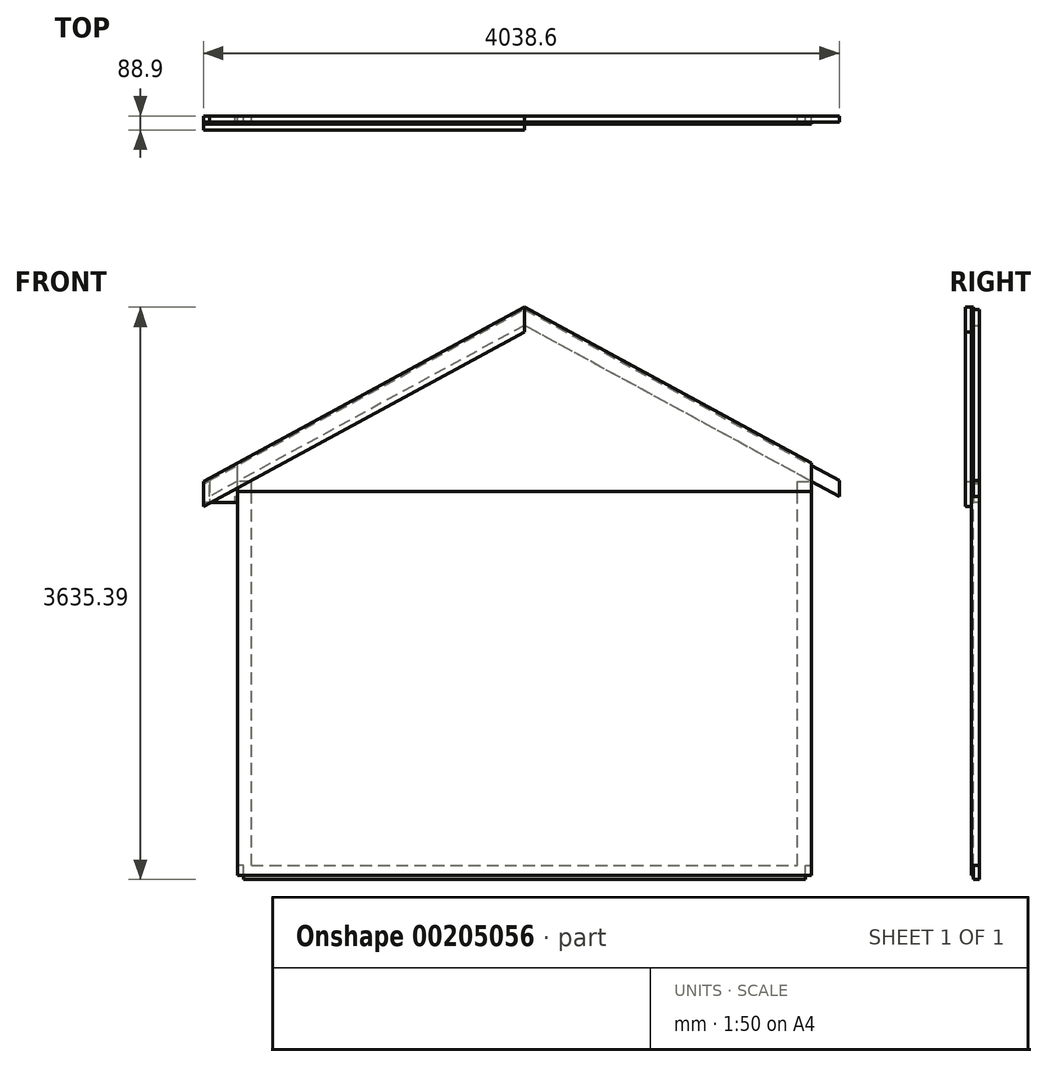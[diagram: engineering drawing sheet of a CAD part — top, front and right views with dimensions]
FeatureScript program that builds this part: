
annotation { "Feature Type Name" : "Feature", "Feature Type Description" : "" }
export const myFeature = defineFeature(function(context is Context, id is Id, definition is map)
    precondition{}
    {
        {
            var Q0;
            Q0=qCreatedBy(makeId("Front.planeOp"),FACE);
            var sketch = newSketch(context, id + "F0", { "sketchPlane" : qUnion([Q0])});
            skLineSegment(sketch, "E0.bottom", {"start": v(-1784.35, 0) * mm, "end": v(1784.35, 0) * mm});
            skLineSegment(sketch, "E0.top", {"start": v(-1784.35, 88.9) * mm, "end": v(1784.35, 88.9) * mm});
            skLineSegment(sketch, "E0.left", {"start": v(-1784.35, 0) * mm, "end": v(-1784.35, 88.9) * mm});
            skLineSegment(sketch, "E0.right", {"start": v(1784.35, 0) * mm, "end": v(1784.35, 88.9) * mm});
            skLineSegment(sketch, "E1.bottom", {"start": v(1733.55, 88.9) * mm, "end": v(1822.45, 88.9) * mm});
            skLineSegment(sketch, "E1.top", {"start": v(1733.55, 2528.73) * mm, "end": v(1822.45, 2528.73) * mm});
            skLineSegment(sketch, "E1.left", {"start": v(1733.55, 88.9) * mm, "end": v(1733.55, 2528.73) * mm});
            skLineSegment(sketch, "E1.right", {"start": v(1822.45, 88.9) * mm, "end": v(1822.45, 2528.73) * mm});
            skLineSegment(sketch, "E2.bottom", {"start": v(-1733.55, 88.9) * mm, "end": v(-1822.45, 88.9) * mm});
            skLineSegment(sketch, "E2.top", {"start": v(-1733.55, 2528.73) * mm, "end": v(-1822.45, 2528.73) * mm});
            skLineSegment(sketch, "E2.left", {"start": v(-1733.55, 88.9) * mm, "end": v(-1733.55, 2528.73) * mm});
            skLineSegment(sketch, "E2.right", {"start": v(-1822.45, 88.9) * mm, "end": v(-1822.45, 2528.73) * mm});
            skLineSegment(sketch, "E3", {"start": v(0, 3620.93) * mm, "end": v(2000.25, 2533.24) * mm});
            skLineSegment(sketch, "E4", {"start": v(2000.25, 2533.24) * mm, "end": v(2000.25, 2432.05) * mm});
            skLineSegment(sketch, "E5", {"start": v(2000.25, 2432.05) * mm, "end": v(0, 3519.74) * mm});
            skLineSegment(sketch, "E6", {"start": v(0, 3519.74) * mm, "end": v(-2000.25, 2432.05) * mm});
            skLineSegment(sketch, "E7", {"start": v(-2000.25, 2432.05) * mm, "end": v(-2000.25, 2533.24) * mm});
            skLineSegment(sketch, "E8", {"start": v(-2000.25, 2533.24) * mm, "end": v(0, 3620.93) * mm});
            skSolve(sketch);
        }
        {
            var Q0;
            Q0=makeQuery(id+"F0.imprint","IMPRINT",FACE,{"disambiguationData":[TD([[makeQuery(id+"F0.imprint","IMPRINT",EDGE,{"derivedFrom":sQuery(id+"F0.wireOp",EDGE,"E3")}),-1.0]])]});
            var Q1;
            Q1=makeQuery(id+"F0.imprint","IMPRINT",FACE,{"disambiguationData":[TD([[makeQuery(id+"F0.imprint","IMPRINT",EDGE,{"derivedFrom":sQuery(id+"F0.wireOp",EDGE,"E1.top")}),-1.0]])]});
            var Q2;
            Q2=makeQuery(id+"F0.imprint","IMPRINT",FACE,{"disambiguationData":[TD([[makeQuery(id+"F0.imprint","IMPRINT",EDGE,{"derivedFrom":sQuery(id+"F0.wireOp",EDGE,"E2.top")}),1.0]])]});
            var Q3;
            Q3=makeQuery(id+"F0.imprint","IMPRINT",FACE,{"disambiguationData":[TD([[makeQuery(id+"F0.imprint","IMPRINT",EDGE,{"derivedFrom":sQuery(id+"F0.wireOp",EDGE,"E0.bottom")}),1.0]])]});
            extrude(context, id + "F1", {"entities" : qUnion([Q0, Q1, Q2, Q3]), "depth" : 38.1 * mm});
        }
        {
            var Q0;
            Q0=makeQuery(id+"F1.opExtrude","CAP_FACE",FACE,{"disambiguationData":[OSD([sQuery(id+"F0.wireOp",EDGE,"E0.bottom"),sQuery(id+"F0.wireOp",EDGE,"E0.top"),sQuery(id+"F0.wireOp",EDGE,"E0.left"),sQuery(id+"F0.wireOp",EDGE,"E0.right"),sQuery(id+"F0.wireOp",EDGE,"E1.bottom"),sQuery(id+"F0.wireOp",EDGE,"E1.top"),sQuery(id+"F0.wireOp",EDGE,"E1.left"),sQuery(id+"F0.wireOp",EDGE,"E1.right"),sQuery(id+"F0.wireOp",EDGE,"E2.bottom"),sQuery(id+"F0.wireOp",EDGE,"E2.top"),sQuery(id+"F0.wireOp",EDGE,"E2.left"),sQuery(id+"F0.wireOp",EDGE,"E2.right")])],"isStart":false});
            var sketch = newSketch(context, id + "F2", { "sketchPlane" : qUnion([Q0])});
            skLineSegment(sketch, "E9.bottom", {"start": v(-1822.45, 25.4) * mm, "end": v(1822.45, 25.4) * mm});
            skLineSegment(sketch, "E9.top", {"start": v(-1822.45, 2463.8) * mm, "end": v(1822.45, 2463.8) * mm});
            skLineSegment(sketch, "E9.left", {"start": v(-1822.45, 25.4) * mm, "end": v(-1822.45, 2463.8) * mm});
            skLineSegment(sketch, "E9.right", {"start": v(1822.45, 25.4) * mm, "end": v(1822.45, 2463.8) * mm});
            skSolve(sketch);
        }
        {
            var Q0;
            Q0 = qSketchRegion(id + "F2", true);
            extrude(context, id + "F3", {"entities" : qUnion([Q0]), "depth" : 12.7 * mm});
        }
        {
            var Q0;
            Q0=makeQuery(id+"F1.opExtrude","CAP_FACE",FACE,{"disambiguationData":[OSD([sQuery(id+"F0.wireOp",EDGE,"E3"),sQuery(id+"F0.wireOp",EDGE,"E4"),sQuery(id+"F0.wireOp",EDGE,"E5"),sQuery(id+"F0.wireOp",EDGE,"E6"),sQuery(id+"F0.wireOp",EDGE,"E7"),sQuery(id+"F0.wireOp",EDGE,"E8")])],"isStart":false});
            var sketch = newSketch(context, id + "F4", { "sketchPlane" : qUnion([Q0])});
            skLineSegment(sketch, "E10", {"start": v(-1822.45, 2463.8) * mm, "end": v(-1822.45, 2644.38) * mm});
            skLineSegment(sketch, "E11", {"start": v(-1822.45, 2644.38) * mm, "end": v(0, 3635.39) * mm});
            skLineSegment(sketch, "E12", {"start": v(0, 3635.39) * mm, "end": v(1822.45, 2644.38) * mm});
            skLineSegment(sketch, "E13", {"start": v(1822.45, 2644.38) * mm, "end": v(1822.45, 2463.8) * mm});
            skLineSegment(sketch, "E14", {"start": v(1822.45, 2463.8) * mm, "end": v(-1822.45, 2463.8) * mm});
            skSolve(sketch);
        }
        {
            var Q0;
            Q0 = qSketchRegion(id + "F4", true);
            extrude(context, id + "F5", {"entities" : qUnion([Q0]), "depth" : 12.7 * mm});
        }
        {
            var Q0;
            Q0=makeQuery(id+"F1.opExtrude","CAP_FACE",FACE,{"disambiguationData":[OSD([sQuery(id+"F0.wireOp",EDGE,"E3"),sQuery(id+"F0.wireOp",EDGE,"E4"),sQuery(id+"F0.wireOp",EDGE,"E5"),sQuery(id+"F0.wireOp",EDGE,"E6"),sQuery(id+"F0.wireOp",EDGE,"E7"),sQuery(id+"F0.wireOp",EDGE,"E8")])],"isStart":false});
            var sketch = newSketch(context, id + "F6", { "sketchPlane" : qUnion([Q0])});
            skLineSegment(sketch, "E15", {"start": v(-2000.25, 2533.24) * mm, "end": v(-2000.25, 2393.54) * mm});
            skLineSegment(sketch, "E16", {"start": v(-2000.25, 2393.54) * mm, "end": v(-2038.35, 2393.54) * mm});
            skLineSegment(sketch, "E17", {"start": v(-2038.35, 2393.54) * mm, "end": v(-2038.35, 2512.53) * mm});
            skLineSegment(sketch, "E18", {"start": v(-2038.35, 2512.53) * mm, "end": v(-2000.25, 2533.24) * mm});
            skSolve(sketch);
        }
        {
            var Q0;
            Q0 = qSketchRegion(id + "F6", true);
            extrude(context, id + "F7", {"entities" : qUnion([Q0]), "oppositeDirection" : true, "depth" : 38.1 * mm});
        }
        {
            var Q0;
            Q0=makeQuery(id+"F7.boolean.opBoolean","MERGE",FACE,{"derivedFrom":[makeQuery(id+"F1.opExtrude","CAP_FACE",FACE,{"disambiguationData":[OSD([sQuery(id+"F0.wireOp",EDGE,"E3"),sQuery(id+"F0.wireOp",EDGE,"E4"),sQuery(id+"F0.wireOp",EDGE,"E5"),sQuery(id+"F0.wireOp",EDGE,"E6"),sQuery(id+"F0.wireOp",EDGE,"E7"),sQuery(id+"F0.wireOp",EDGE,"E8")])],"isStart":false}),makeQuery(id+"F7.opExtrude","CAP_FACE",FACE,{"disambiguationData":[OSD([sQuery(id+"F6.wireOp",EDGE,"E15"),sQuery(id+"F6.wireOp",EDGE,"E16"),sQuery(id+"F6.wireOp",EDGE,"E17"),sQuery(id+"F6.wireOp",EDGE,"E18")])],"isStart":true})]});
            var sketch = newSketch(context, id + "F8", { "sketchPlane" : qUnion([Q0])});
            skLineSegment(sketch, "E19.bottom", {"start": v(-1841.5, 2431.64) * mm, "end": v(-1822.45, 2431.64) * mm});
            skLineSegment(sketch, "E19.top", {"start": v(-1841.5, 2393.54) * mm, "end": v(-1822.45, 2393.54) * mm});
            skLineSegment(sketch, "E19.left", {"start": v(-1841.5, 2431.64) * mm, "end": v(-1841.5, 2393.54) * mm});
            skLineSegment(sketch, "E19.right", {"start": v(-1822.45, 2431.64) * mm, "end": v(-1822.45, 2393.54) * mm});
            skSolve(sketch);
        }
        {
            var Q0;
            Q0 = qSketchRegion(id + "F8", true);
            extrude(context, id + "F9", {"entities" : qUnion([Q0]), "operationType" : NewBodyOperationType.ADD, "oppositeDirection" : true, "depth" : 38.1 * mm});
        }
        {
            var Q0;
            Q0=makeQuery(id+"F5.opExtrude","CAP_FACE",FACE,{"disambiguationData":[OSD([sQuery(id+"F4.wireOp",EDGE,"E10"),sQuery(id+"F4.wireOp",EDGE,"E11"),sQuery(id+"F4.wireOp",EDGE,"E12"),sQuery(id+"F4.wireOp",EDGE,"E13"),sQuery(id+"F4.wireOp",EDGE,"E14")])],"isStart":false});
            var sketch = newSketch(context, id + "F10", { "sketchPlane" : qUnion([Q0])});
            skLineSegment(sketch, "E20", {"start": v(0, 3635.39) * mm, "end": v(0, 3476.37) * mm});
            skLineSegment(sketch, "E21", {"start": v(0, 3476.37) * mm, "end": v(-2038.35, 2367.96) * mm});
            skLineSegment(sketch, "E22", {"start": v(-2038.35, 2367.96) * mm, "end": v(-2038.35, 2526.98) * mm});
            skLineSegment(sketch, "E23", {"start": v(-2038.35, 2526.98) * mm, "end": v(0, 3635.39) * mm});
            skSolve(sketch);
        }
        {
            var Q0;
            Q0 = qSketchRegion(id + "F10", true);
            extrude(context, id + "F11", {"entities" : qUnion([Q0]), "depth" : 38.1 * mm});
        }
        {
            var Q0;
            Q0=makeQuery(id+"F7.opExtrude","CAP_FACE",FACE,{"disambiguationData":[OSD([sQuery(id+"F6.wireOp",EDGE,"E15"),sQuery(id+"F6.wireOp",EDGE,"E16"),sQuery(id+"F6.wireOp",EDGE,"E17"),sQuery(id+"F6.wireOp",EDGE,"E18")])],"isStart":true});
            var sketch = newSketch(context, id + "F12", { "sketchPlane" : qUnion([Q0])});
            skLineSegment(sketch, "E24", {"start": v(-2038.35, 2526.98) * mm, "end": v(-2038.35, 2393.54) * mm});
            skLineSegment(sketch, "E25", {"start": v(-2038.35, 2393.54) * mm, "end": v(-1822.45, 2393.54) * mm});
            skLineSegment(sketch, "E26", {"start": v(-1822.45, 2393.54) * mm, "end": v(-1822.45, 2644.38) * mm});
            skLineSegment(sketch, "E27", {"start": v(-1822.45, 2644.38) * mm, "end": v(-2038.35, 2526.98) * mm});
            skSolve(sketch);
        }
        {
            var Q0;
            Q0 = qSketchRegion(id + "F12", true);
            extrude(context, id + "F13", {"entities" : qUnion([Q0]), "depth" : 12.7 * mm});
        }
    });
